# Revit family: 05-7830-21-M1
name_source: partatom
category: Luminarias
revit_build: Autodesk Revit 2017 (Build: 20160225_1515(x64)
units: mm (PartAtom-declared; Revit-internal decimal feet)

## family parameters
Compartido = Sí
Corte con vacíos al cargar = No
Cota de conector redondo = Diámetro de uso
Número OmniClass = 23.80.70.00
Origen de luz = No
Punto de cálculo de habitación = No
Se basa en plano de trabajo = No
Siempre vertical = Sí
Tipo de pieza = Normal
Título OmniClass = Lighting

## types (1)
- 05-7830-21-M1
    Acabado = Cromo, Arenado
    CRI = 80
    Catálogo = Decorative
    CodigoGubimclass = 50.60.50.20
    CodigoOmniclass = 21-04 50 40
    CodigoUniclass2015 = EF_70_80
    CodigoUniformat2010 = D5040
    DescripcionGubimclass = Iluminación interior
    DescripcionOmniclass = Lighting
    DescripcionUniclass2015 = Lighting
    DescripcionUniformat2010 = Lighting
    EAN13 = 8435575314931
    Eficiencia energética = LED A++
    Etiqueta V/f = 220-240V/50-60Hz
    Fabricante = LEDS C4
    Familia = Toi LED Small
    FechaVersion = Julio 2020
    Ficha = http://files.leds-c4.com
    Fotometría = http://files.leds-c4.com
    IMC = http://files.leds-c4.com
    IP = IP44
    IfcExportAs = IfcLightFixture
    IfcExportType = NOTDEFINED
    Imagen web = http://files.leds-c4.com
    LDT = http://files.leds-c4.com
    Lumenes reales (lm) = 661
    Material = Aluminio, Policarbonato
    Peso neto (KG) = 0.52
    Producto descatalogado = Catalogado ES
    Referencia = 05-7830-21-M1
    Temperatura color led (K) = Blanco cálido - 3000K
    Tender text (Castellano) = LEDS C4
Toi LED Small
05-7830-21-M1

Aplique de uso interior para iluminar frontalmente 
Material estructura: Aluminio. Acabado estructura: Cromo. Material difusor: Policarbonato. Acabado difusor: Arenado. Garantía: 5 Años.

Peso neto del producto (Kg): 0.520
Longitud del producto (mm): 315
Anchura o diámetro del producto (mm): 45
Salida del producto (mm): 81.5

Clase 1. IP: IP44. LED. Nº de portalámparas o Leds: 49. Marca del LED: SAMSUNG. Marca del Driver: TRIDONIC. Potencia máxima de la fuente de luz: 6.7W. Temperatura de color: Blanco cálido - 3000K. Índice de reproducción cromática: 80. Steps Mac Adam: 3. Diámetro máximo de la bombilla que admite la luminaria: 50.000h L80B20. UGR:  16.9. Riesgo fotobiológico: RG0. % de Flickering: &lt;5%. Flujo real (lm): 661. Lm/W reales: 76. Rango de voltaje/frecuencia: 220-240/50-60Hz. Voltaje: 3. Equipo incluido: Si, electrónico. Potencia total: 8.7. Factor de potencia: 0.80.
    Tender text (English) = LEDS C4
Toi LED Small
05-7830-21-M1

Wall light for indoor use. 

For frontal lighting. Structure material: Aluminium. Structure finish: Chrome. Diffuser material: Polycarbonate. Diffuser finish: Sandblasted. Warranty: 5 Years.

Product net weight (Kg): 0.520
Product length (mm): 315
Product width or diameter (mm): 45
Product aperture (mm): 81.5

Class 1. IP: IP44. LED. No. of lampholders or LEDs: 49. LED brand: SAMSUNG. Driver brand: TRIDONIC. Maximum power of light source: 6.7W. Colour temperature: LED warm-white 3000K. Colour rendering index: 80. MacAdam Steps: 3. Maximum diameter of luminaire bulb: 50.000h L80B20. UGR:  16.9. Photobiological risk: RG0. % de Flickering: &lt;5%. Real flux (lm): 661. Lm/Real W: 76. Voltage and frequency range: 220-240/50-60Hz. Voltage: 3. Gear included: Yes, electronic. Total power: 8.7. Power factor: 0.80.
    Tipo = Baño
    Vatios (W) = 8.7
    Versión = v1
